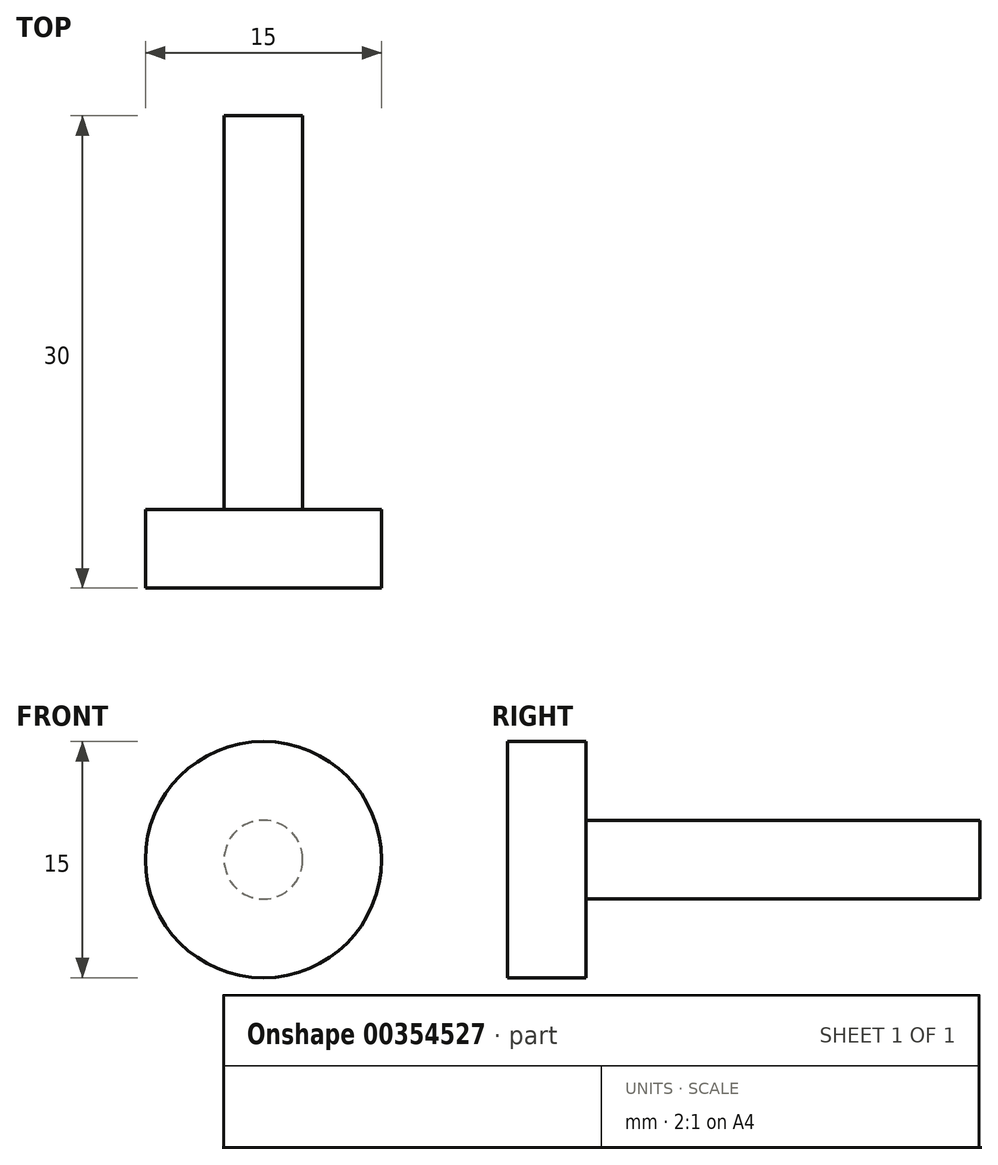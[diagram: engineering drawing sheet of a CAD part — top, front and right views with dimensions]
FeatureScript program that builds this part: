
annotation { "Feature Type Name" : "Feature", "Feature Type Description" : "" }
export const myFeature = defineFeature(function(context is Context, id is Id, definition is map)
    precondition{}
    {
        {
            var Q0;
            Q0=qCreatedBy(makeId("Front.planeOp"),FACE);
            var sketch = newSketch(context, id + "F0", { "sketchPlane" : qUnion([Q0])});
            skCircle(sketch, "E0", {"center": v(0, 0) * mm, "radius": 2.5 * mm});
            skSolve(sketch);
        }
        {
            var Q0;
            Q0=makeQuery(id+"F0.imprint","IMPRINT",FACE,{"disambiguationData":[TD([[makeQuery(id+"F0.imprint","IMPRINT",EDGE,{"derivedFrom":sQuery(id+"F0.wireOp",EDGE,"E0")}),1.0]])]});
            extrude(context, id + "F1", {"entities" : qUnion([Q0]), "depth" : 25 * mm, "offsetDistance" : 25 * mm});
        }
        {
            var Q0;
            Q0=makeQuery(id+"F1.opExtrude","CAP_FACE",FACE,{"disambiguationData":[OSD([sQuery(id+"F0.wireOp",EDGE,"E0")])],"isStart":false});
            var sketch = newSketch(context, id + "F2", { "sketchPlane" : qUnion([Q0])});
            skCircle(sketch, "E1", {"center": v(0, 0) * mm, "radius": 7.5 * mm});
            skSolve(sketch);
        }
        {
            var Q0;
            Q0 = qSketchRegion(id + "F2", true);
            extrude(context, id + "F3", {"entities" : qUnion([Q0]), "operationType" : NewBodyOperationType.ADD, "depth" : 5 * mm, "offsetDistance" : 25 * mm});
        }
    });
